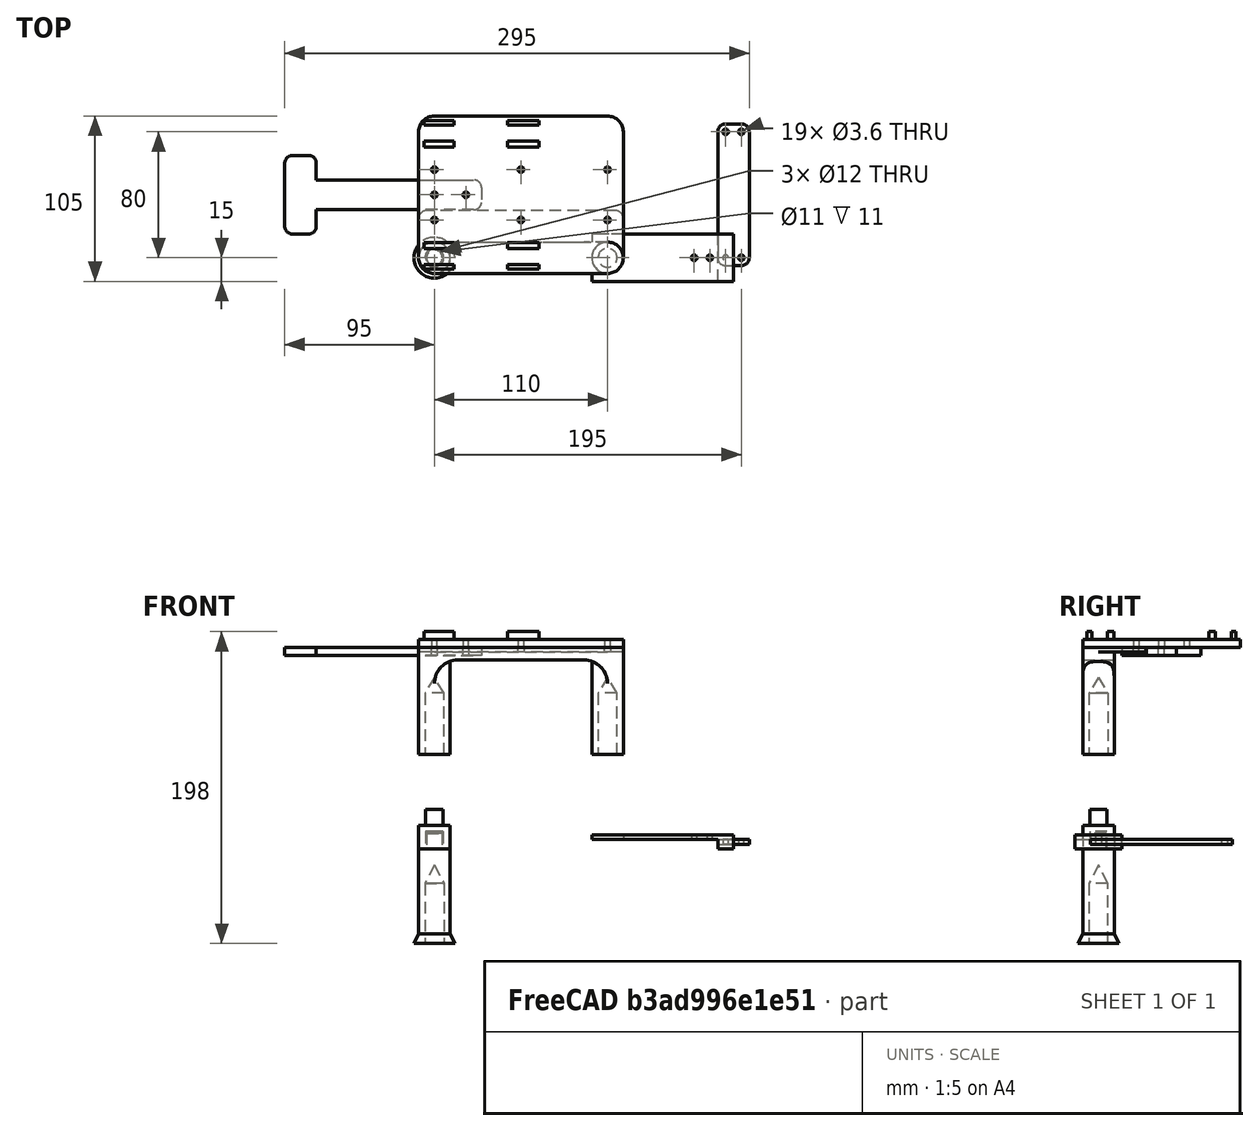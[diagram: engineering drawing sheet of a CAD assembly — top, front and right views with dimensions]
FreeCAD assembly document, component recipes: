
FREECAD ASSEMBLY — COMPONENT RECIPES ("Support_long")

This assembly document has 9 components, labeled P0..P8 below (a component is one placed body or linked part). 9 of them carry a construction recipe — the FreeCAD feature program that regenerates the part from scratch, quoted from this document or its linked companion documents; the rest are supplied as boundary geometry only. No exploded tour is included for this assembly.
COMPONENT P0 — recipe-attached ("Top", modeled in this document).
Construction recipe (the document's own serialized feature program — sketch geometry with constraints, then the solid features built on it; lengths are millimeters unless a unit is written):

FEATURE [Sketcher::SketchObject] Sketch
  ArcFitTolerance = 0
  AttachmentSupport = -> [XY_Plane]
  FullyConstrained = true
  MakeInternals = false
  MapMode = 5
  sketch-geometry (29):
    g0: LineSegment [constr] StartX=0 StartY=100 StartZ=0 EndX=130 EndY=100 EndZ=0
    g1: LineSegment [constr] StartX=130 StartY=100 StartZ=0 EndX=130 EndY=0 EndZ=0
    g2: LineSegment [constr] StartX=130 StartY=0 StartZ=0 EndX=0 EndY=0 EndZ=0
    g3: LineSegment [constr] StartX=0 StartY=0 StartZ=0 EndX=0 EndY=100 EndZ=0
    g4: LineSegment [constr] StartX=10 StartY=66 StartZ=0 EndX=120 EndY=66 EndZ=0
    g5: LineSegment [constr] StartX=120 StartY=66 StartZ=0 EndX=120 EndY=34 EndZ=0
    g6: LineSegment [constr] StartX=120 StartY=34 StartZ=0 EndX=10 EndY=34 EndZ=0
    g7: LineSegment [constr] StartX=10 StartY=34 StartZ=0 EndX=10 EndY=66 EndZ=0
    g8: LineSegment [constr] StartX=130 StartY=100 StartZ=0 EndX=120 EndY=66 EndZ=0
    g9: LineSegment [constr] StartX=120 StartY=34 StartZ=0 EndX=130 EndY=0 EndZ=0
    g10: LineSegment [constr] StartX=10 StartY=66 StartZ=0 EndX=0 EndY=100 EndZ=0
    g11: Circle CenterX=120 CenterY=66 CenterZ=0 NormalX=0 NormalY=0 NormalZ=1 AngleXU=0 Radius=1.8
    g12: Circle CenterX=120 CenterY=34 CenterZ=0 NormalX=0 NormalY=0 NormalZ=1 AngleXU=0 Radius=1.8
    g13: Circle CenterX=10 CenterY=34 CenterZ=0 NormalX=0 NormalY=0 NormalZ=1 AngleXU=0 Radius=1.8
    g14: Circle CenterX=10 CenterY=66 CenterZ=0 NormalX=0 NormalY=0 NormalZ=1 AngleXU=0 Radius=1.8
    g15: Circle CenterX=10 CenterY=50 CenterZ=0 NormalX=0 NormalY=0 NormalZ=1 AngleXU=0 Radius=1.8
    g16: Circle CenterX=30 CenterY=50 CenterZ=0 NormalX=0 NormalY=0 NormalZ=1 AngleXU=0 Radius=1.8
    g17: LineSegment [constr] StartX=0 StartY=100 StartZ=0 EndX=10 EndY=50 EndZ=0
    g18: LineSegment [constr] StartX=10 StartY=50 StartZ=0 EndX=0 EndY=0 EndZ=0
    g19: LineSegment StartX=0 StartY=90 StartZ=0 EndX=0 EndY=10 EndZ=0
    g20: LineSegment StartX=10 StartY=0 StartZ=0 EndX=120 EndY=0 EndZ=0
    g21: LineSegment StartX=130 StartY=10 StartZ=0 EndX=130 EndY=90 EndZ=0
    g22: LineSegment StartX=120 StartY=100 StartZ=0 EndX=10 EndY=100 EndZ=0
    g23: ArcOfCircle CenterX=10 CenterY=90 CenterZ=0 NormalX=0 NormalY=0 NormalZ=1 AngleXU=0 Radius=10 StartAngle=1.5708 EndAngle=3.14159
    g24: ArcOfCircle CenterX=120 CenterY=90 CenterZ=0 NormalX=0 NormalY=0 NormalZ=1 AngleXU=0 Radius=10 StartAngle=0 EndAngle=1.5708
    g25: ArcOfCircle CenterX=120 CenterY=10 CenterZ=0 NormalX=0 NormalY=0 NormalZ=1 AngleXU=0 Radius=10 StartAngle=4.71239 EndAngle=6.28319
    g26: ArcOfCircle CenterX=10 CenterY=10 CenterZ=0 NormalX=0 NormalY=0 NormalZ=1 AngleXU=0 Radius=10 StartAngle=3.14159 EndAngle=4.71239
    g27: Circle CenterX=65 CenterY=66 CenterZ=0 NormalX=0 NormalY=0 NormalZ=1 AngleXU=0 Radius=1.8
    g28: Circle CenterX=65 CenterY=34 CenterZ=0 NormalX=0 NormalY=0 NormalZ=1 AngleXU=0 Radius=1.8
  constraints (82):
    c: Coincident(g0,g1)
    c: Coincident(g1,g2)
    c: Coincident(g2,g3)
    c: Coincident(g3,g0)
    c: Horizontal(g0)
    c: Horizontal(g2)
    c: Vertical(g1)
    c: Vertical(g3)
    c: DistanceY(g1,g1) = 100
    c: DistanceX(g2,g2) = 130
    c: DistanceX(g2) = 0
    c: DistanceY(g2) = 0
    c: Coincident(g4,g5)
    c: Coincident(g5,g6)
    c: Coincident(g6,g7)
    c: Coincident(g7,g4)
    c: Horizontal(g4)
    c: Horizontal(g6)
    c: Vertical(g5)
    c: Vertical(g7)
    c: DistanceX(g4,g4) = 110
    c: DistanceY(g7,g7) = 32
    c: Coincident(g8,g0)
    c: Coincident(g8,g4)
    c: Coincident(g9,g5)
    c: Coincident(g9,g1)
    c: Coincident(g10,g4)
    c: Coincident(g10,g0)
    c: Equal(g10,g8)
    c: Equal(g8,g9)
    c: Coincident(g11,g4)
    c: Coincident(g12,g5)
    c: Coincident(g13,g6)
    c: Coincident(g14,g4)
    c: Equal(g14,g13)
    c: Equal(g13,g11)
    c: Equal(g11,g12)
    c: Radius(g14) = 1.8
    c: DistanceY(g16,g15) = 0
    c: DistanceX(g15,g16) = 20
    c: DistanceX(g2,g15) = 10
    c: Coincident(g17,g0)
    c: Coincident(g17,g15)
    c: Coincident(g18,g15)
    c: Coincident(g18,g2)
    c: Equal(g18,g17)
    c: Equal(g16,g15)
    c: Radius(g16) = 1.8
    c: Vertical(g19)
    c: Vertical(g21)
    c: Horizontal(g20)
    c: Horizontal(g22)
    c: Coincident(g23,g22)
    c: Coincident(g23,g19)
    c: Coincident(g24,g22)
    c: Coincident(g24,g21)
    c: Coincident(g25,g21)
    c: Coincident(g25,g20)
    c: Coincident(g26,g19)
    c: Coincident(g26,g20)
    c: DistanceX(g19,g2) = 0
    c: DistanceX(g19,g21) = 130
    c: DistanceY(g20,g2) = 0
    c: DistanceY(g20,g22) = 100
    c: DistanceX(g22,g23) = 0
    c: DistanceX(g24,g22) = 0
    c: DistanceX(g20,g25) = 0
    c: DistanceX(g20,g26) = 0
    c: DistanceY(g23,g19) = 0
    c: DistanceY(g24,g21) = 0
    c: DistanceY(g21,g25) = 0
    c: DistanceY(g19,g26) = 0
    c: Equal(g23,g24)
    c: Equal(g24,g25)
    c: Equal(g25,g26)
    c: Radius(g23) = 10
    c: DistanceY(g27,g4) = 0
    c: DistanceY(g5,g28) = 0
    c: DistanceX(g27,g28) = 0
    c: Equal(g27,g28)
    c: Equal(g28,g14)
    c: DistanceX(g27,g4) = 55
FEATURE [PartDesign::Pad] Pad
  Direction = (0,0,1)
  Length = 5
  Length2 = 10
  Profile = -> Sketch
  ReferenceAxis = -> Sketch [N_Axis]
  Suppressed = false
  Type = 0
FEATURE [Sketcher::SketchObject] Sketch001
  ArcFitTolerance = 0
  AttachmentOffset = pos=(0,0,5) rot=(0,0,1;0rad)
  AttachmentSupport = -> [XY_Plane]
  FullyConstrained = true
  MakeInternals = false
  MapMode = 5
  Placement = pos=(0,0,5) rot=(0,0,1;0rad)
  sketch-geometry (39):
    g0: LineSegment StartX=56.5 StartY=84.25 StartZ=0 EndX=76.5 EndY=84.25 EndZ=0
    g1: LineSegment StartX=76.5 StartY=84.25 StartZ=0 EndX=76.5 EndY=80.25 EndZ=0
    g2: LineSegment StartX=76.5 StartY=80.25 StartZ=0 EndX=56.5 EndY=80.25 EndZ=0
    g3: LineSegment StartX=56.5 StartY=80.25 StartZ=0 EndX=56.5 EndY=84.25 EndZ=0
    g4: LineSegment StartX=56.5 StartY=19.75 StartZ=0 EndX=76.5 EndY=19.75 EndZ=0
    g5: LineSegment StartX=76.5 StartY=19.75 StartZ=0 EndX=76.5 EndY=15.75 EndZ=0
    g6: LineSegment StartX=76.5 StartY=15.75 StartZ=0 EndX=56.5 EndY=15.75 EndZ=0
    g7: LineSegment StartX=56.5 StartY=15.75 StartZ=0 EndX=56.5 EndY=19.75 EndZ=0
    g8: LineSegment [constr] StartX=80 StartY=100 StartZ=0 EndX=0 EndY=100 EndZ=0
    g9: LineSegment [constr] StartX=0 StartY=100 StartZ=0 EndX=0 EndY=0 EndZ=0
    g10: LineSegment [constr] StartX=0 StartY=0 StartZ=0 EndX=80 EndY=0 EndZ=0
    g11: LineSegment [constr] StartX=80 StartY=0 StartZ=0 EndX=80 EndY=100 EndZ=0
    g12: LineSegment StartX=3.5 StartY=84.25 StartZ=0 EndX=22.5 EndY=84.25 EndZ=0
    g13: LineSegment StartX=22.5 StartY=84.25 StartZ=0 EndX=22.5 EndY=80.25 EndZ=0
    g14: LineSegment StartX=22.5 StartY=80.25 StartZ=0 EndX=3.5 EndY=80.25 EndZ=0
    g15: LineSegment StartX=3.5 StartY=80.25 StartZ=0 EndX=3.5 EndY=84.25 EndZ=0
    g16: LineSegment StartX=3.5 StartY=19.75 StartZ=0 EndX=22.5 EndY=19.75 EndZ=0
    g17: LineSegment StartX=22.5 StartY=19.75 StartZ=0 EndX=22.5 EndY=15.75 EndZ=0
    g18: LineSegment StartX=22.5 StartY=15.75 StartZ=0 EndX=3.5 EndY=15.75 EndZ=0
    g19: LineSegment StartX=3.5 StartY=15.75 StartZ=0 EndX=3.5 EndY=19.75 EndZ=0
    g20: LineSegment [constr] StartX=3.5 StartY=84.25 StartZ=0 EndX=0 EndY=100 EndZ=0
    g21: LineSegment [constr] StartX=76.5 StartY=84.25 StartZ=0 EndX=80 EndY=100 EndZ=0
    g22: LineSegment [constr] StartX=76.5 StartY=15.75 StartZ=0 EndX=80 EndY=0 EndZ=0
    g23: LineSegment StartX=3.5 StartY=97.25 StartZ=0 EndX=22.5 EndY=97.25 EndZ=0
    g24: LineSegment StartX=22.5 StartY=97.25 StartZ=0 EndX=22.5 EndY=94.25 EndZ=0
    g25: LineSegment StartX=22.5 StartY=94.25 StartZ=0 EndX=3.5 EndY=94.25 EndZ=0
    g26: LineSegment StartX=3.5 StartY=94.25 StartZ=0 EndX=3.5 EndY=97.25 EndZ=0
    g27: LineSegment StartX=56.5 StartY=97.25 StartZ=0 EndX=76.5 EndY=97.25 EndZ=0
    g28: LineSegment StartX=76.5 StartY=97.25 StartZ=0 EndX=76.5 EndY=94.25 EndZ=0
    g29: LineSegment StartX=76.5 StartY=94.25 StartZ=0 EndX=56.5 EndY=94.25 EndZ=0
    g30: LineSegment StartX=56.5 StartY=94.25 StartZ=0 EndX=56.5 EndY=97.25 EndZ=0
    g31: LineSegment StartX=56.5 StartY=5.75 StartZ=0 EndX=76.5 EndY=5.75 EndZ=0
    g32: LineSegment StartX=76.5 StartY=5.75 StartZ=0 EndX=76.5 EndY=2.75 EndZ=0
    g33: LineSegment StartX=76.5 StartY=2.75 StartZ=0 EndX=56.5 EndY=2.75 EndZ=0
    g34: LineSegment StartX=56.5 StartY=2.75 StartZ=0 EndX=56.5 EndY=5.75 EndZ=0
    g35: LineSegment StartX=22.5 StartY=5.75 StartZ=0 EndX=3.5 EndY=5.75 EndZ=0
    g36: LineSegment StartX=3.5 StartY=5.75 StartZ=0 EndX=3.5 EndY=2.75 EndZ=0
    g37: LineSegment StartX=3.5 StartY=2.75 StartZ=0 EndX=22.5 EndY=2.75 EndZ=0
    g38: LineSegment StartX=22.5 StartY=2.75 StartZ=0 EndX=22.5 EndY=5.75 EndZ=0
  constraints (114):
    c: Coincident(g0,g1)
    c: Coincident(g1,g2)
    c: Coincident(g2,g3)
    c: Coincident(g3,g0)
    c: Horizontal(g0)
    c: Horizontal(g2)
    c: Vertical(g1)
    c: Vertical(g3)
    c: Coincident(g4,g5)
    c: Coincident(g5,g6)
    c: Coincident(g6,g7)
    c: Coincident(g7,g4)
    c: Horizontal(g4)
    c: Horizontal(g6)
    c: Vertical(g5)
    c: Vertical(g7)
    c: DistanceY(g1,g1) = 4
    c: DistanceY(g5,g5) = 4
    c: DistanceY(g4,g1) = 60.5
    c: Coincident(g8,g9)
    c: Coincident(g9,g10)
    c: Coincident(g10,g11)
    c: Coincident(g11,g8)
    c: Horizontal(g8)
    c: Horizontal(g10)
    c: Vertical(g9)
    c: Vertical(g11)
    c: DistanceX(g8,g8) = 80
    c: DistanceY(g11,g11) = 100
    c: DistanceX(g9) = 0
    c: DistanceY(g9) = 0
    c: DistanceX(g2,g2) = 20
    c: DistanceX(g1,g4) = 0
    c: DistanceX(g2,g4) = 0
    c: Coincident(g12,g13)
    c: Coincident(g13,g14)
    c: Coincident(g14,g15)
    c: Coincident(g15,g12)
    c: Horizontal(g12)
    c: Horizontal(g14)
    c: Vertical(g13)
    c: Vertical(g15)
    c: Coincident(g16,g17)
    c: Coincident(g17,g18)
    c: Coincident(g18,g19)
    c: Coincident(g19,g16)
    c: Horizontal(g16)
    c: Horizontal(g18)
    c: Vertical(g17)
    c: Vertical(g19)
    c: DistanceX(g12,g12) = 19
    c: DistanceY(g12,g0) = 0
    c: DistanceY(g13,g2) = 0
    c: DistanceY(g4,g16) = 0
    c: DistanceY(g17,g6) = 0
    c: DistanceX(g13,g16) = 0
    c: DistanceX(g14,g16) = 0
    c: DistanceX(g12,g0) = 34
    c: Coincident(g20,g12)
    c: Coincident(g20,g8)
    c: Coincident(g21,g0)
    c: Coincident(g21,g8)
    c: Coincident(g22,g5)
    c: Coincident(g22,g10)
    c: Equal(g20,g21)
    c: Equal(g21,g22)
    c: Coincident(g23,g24)
    c: Coincident(g24,g25)
    c: Coincident(g25,g26)
    c: Coincident(g26,g23)
    c: Horizontal(g23)
    c: Horizontal(g25)
    c: Vertical(g24)
    c: Vertical(g26)
    c: Coincident(g27,g28)
    c: Coincident(g28,g29)
    c: Coincident(g29,g30)
    c: Coincident(g30,g27)
    c: Horizontal(g27)
    c: Horizontal(g29)
    c: Vertical(g28)
    c: Vertical(g30)
    c: Coincident(g31,g32)
    c: Coincident(g32,g33)
    c: Coincident(g33,g34)
    c: Coincident(g34,g31)
    c: Horizontal(g31)
    c: Horizontal(g33)
    c: Vertical(g32)
    c: Vertical(g34)
    c: Coincident(g35,g36)
    c: Coincident(g36,g37)
    c: Coincident(g37,g38)
    c: Coincident(g38,g35)
    c: Horizontal(g35)
    c: Horizontal(g37)
    c: Vertical(g36)
    c: Vertical(g38)
    c: DistanceY(g31,g6) = 10
    c: DistanceY(g35,g31) = 0
    c: DistanceY(g37,g33) = 0
    c: DistanceY(g0,g29) = 10
    c: DistanceY(g24,g29) = 0
    c: DistanceY(g27,g23) = 0
    c: DistanceY(g28,g28) = 3
    c: DistanceY(g32,g32) = 3
    c: DistanceX(g31,g5) = 0
    c: DistanceX(g6,g31) = 0
    c: DistanceX(g18,g35) = 0
    c: DistanceX(g35,g17) = 0
    c: DistanceX(g24,g12) = 0
    c: DistanceX(g12,g25) = 0
    c: DistanceX(g0,g29) = 0
    c: DistanceX(g0,g28) = 0
FEATURE [PartDesign::Pad] Pad001
  BaseFeature = -> Pad
  Direction = (0,0,1)
  Length = 5
  Length2 = 10
  Profile = -> Sketch001
  ReferenceAxis = -> Sketch001 [N_Axis]
  Suppressed = false
  Type = 0
FEATURE [PartDesign::Body] Body  label="Top"
  AllowCompound = false
  Group = -> [Sketch,Pad,Sketch001,Pad001]
  Origin = -> Origin
  Tip = -> Pad001
COMPONENT P1 — recipe-attached ("Stick", modeled in this document).
Construction recipe (the document's own serialized feature program — sketch geometry with constraints, then the solid features built on it; lengths are millimeters unless a unit is written):

FEATURE [Sketcher::SketchObject] Sketch007
  ArcFitTolerance = 0
  AttachmentSupport = -> [XY_Plane003]
  FullyConstrained = true
  MakeInternals = false
  MapMode = 5
  sketch-geometry (18):
    g0: LineSegment StartX=-65 StartY=59.5 StartZ=0 EndX=35 EndY=59.5 EndZ=0
    g1: LineSegment StartX=40 StartY=54.5 StartZ=0 EndX=40 EndY=45.5 EndZ=0
    g2: LineSegment StartX=35 StartY=40.5 StartZ=0 EndX=-65 EndY=40.5 EndZ=0
    g3: LineSegment StartX=-85 StartY=30 StartZ=0 EndX=-85 EndY=70 EndZ=0
    g4: Circle CenterX=30 CenterY=50 CenterZ=0 NormalX=0 NormalY=0 NormalZ=1 AngleXU=0 Radius=1.8
    g5: Circle CenterX=10 CenterY=50 CenterZ=0 NormalX=0 NormalY=0 NormalZ=1 AngleXU=0 Radius=1.8
    g6: LineSegment [constr] StartX=30 StartY=50 StartZ=0 EndX=40 EndY=54.5 EndZ=0
    g7: LineSegment [constr] StartX=30 StartY=50 StartZ=0 EndX=40 EndY=45.5 EndZ=0
    g8: ArcOfCircle CenterX=35 CenterY=54.5 CenterZ=0 NormalX=0 NormalY=0 NormalZ=1 AngleXU=0 Radius=5 StartAngle=5e-16 EndAngle=1.5708
    g9: ArcOfCircle CenterX=35 CenterY=45.5 CenterZ=0 NormalX=0 NormalY=0 NormalZ=1 AngleXU=0 Radius=5 StartAngle=4.71239 EndAngle=6.28319
    g10: ArcOfCircle CenterX=-80 CenterY=70 CenterZ=0 NormalX=0 NormalY=0 NormalZ=1 AngleXU=0 Radius=5 StartAngle=1.5708 EndAngle=3.14159
    g11: ArcOfCircle CenterX=-80 CenterY=30 CenterZ=0 NormalX=0 NormalY=0 NormalZ=1 AngleXU=0 Radius=5 StartAngle=3.14159 EndAngle=4.71239
    g12: LineSegment StartX=-65 StartY=59.5 StartZ=0 EndX=-65 EndY=70 EndZ=0
    g13: LineSegment StartX=-70 StartY=75 StartZ=0 EndX=-80 EndY=75 EndZ=0
    g14: LineSegment StartX=-65 StartY=40.5 StartZ=0 EndX=-65 EndY=30 EndZ=0
    g15: LineSegment StartX=-70 StartY=25 StartZ=0 EndX=-80 EndY=25 EndZ=0
    g16: ArcOfCircle CenterX=-70 CenterY=70 CenterZ=0 NormalX=0 NormalY=0 NormalZ=1 AngleXU=0 Radius=5 StartAngle=0 EndAngle=1.5708
    g17: ArcOfCircle CenterX=-70 CenterY=30 CenterZ=0 NormalX=0 NormalY=0 NormalZ=1 AngleXU=0 Radius=5 StartAngle=4.71239 EndAngle=6.28319
  constraints (58):
    c: Horizontal(g0)
    c: Horizontal(g2)
    c: Vertical(g1)
    c: Vertical(g3)
    c: DistanceX(g1) = 40
    c: DistanceY(g5,g4) = 0
    c: DistanceX(g5,g4) = 20
    c: DistanceX(g-1,g5) = 10
    c: Equal(g4,g5)
    c: Radius(g4) = 1.8
    c: DistanceY(g2,g0) = 19
    c: DistanceY(g-1,g5) = 50
    c: Coincident(g6,g4)
    c: Coincident(g6,g1)
    c: Coincident(g7,g4)
    c: Coincident(g7,g1)
    c: Equal(g7,g6)
    c: DistanceX(g3,g1) = 125
    c: Coincident(g8,g0)
    c: Coincident(g8,g1)
    c: Coincident(g9,g1)
    c: Coincident(g9,g2)
    c: DistanceX(g0,g8) = 0
    c: DistanceX(g2,g9) = 0
    c: DistanceY(g8,g1) = 0
    c: DistanceY(g9,g1) = 0
    c: Equal(g8,g9)
    c: Radius(g8) = 5
    c: Coincident(g10,g3)
    c: Coincident(g11,g3)
    c: DistanceY(g3,g10) = 0
    c: DistanceY(g3,g11) = 0
    c: Equal(g10,g11)
    c: Radius(g10) = 5
    c: DistanceX(g10,g10) = 0
    c: DistanceX(g11,g11) = 0
    c: Coincident(g0,g12)
    c: Vertical(g12)
    c: Horizontal(g13)
    c: Coincident(g2,g14)
    c: Vertical(g14)
    c: Horizontal(g15)
    c: DistanceX(g0,g2) = 0
    c: Coincident(g13,g10)
    c: Coincident(g11,g15)
    c: Equal(g12,g14)
    c: DistanceY(g3,g3) = 40
    c: DistanceY(g16,g16) = 0
    c: DistanceX(g16,g16) = 0
    c: DistanceX(g17,g17) = 0
    c: DistanceY(g17,g17) = 0
    c: Equal(g16,g17)
    c: Coincident(g16,g13)
    c: Coincident(g12,g16)
    c: Coincident(g17,g14)
    c: Coincident(g17,g15)
    c: Radius(g16) = 5
    c: DistanceX(g13,g13) = 10
FEATURE [PartDesign::Pad] Pad006
  Direction = (0,0,1)
  Length = 5
  Length2 = 10
  Profile = -> Sketch007
  ReferenceAxis = -> Sketch007 [N_Axis]
  Reversed = true
  Suppressed = false
  Type = 0
FEATURE [PartDesign::Body] Body003  label="Stick"
  AllowCompound = false
  Group = -> [Sketch007,Pad006]
  Origin = -> Origin003
  Tip = -> Pad006
COMPONENT P2 — recipe-attached ("Cross", modeled in this document).
Construction recipe (the document's own serialized feature program — sketch geometry with constraints, then the solid features built on it; lengths are millimeters unless a unit is written):

FEATURE [Sketcher::SketchObject] Sketch010
  ArcFitTolerance = 1e-06
  AttachmentSupport = -> [XY_Plane005]
  FullyConstrained = true
  MakeInternals = false
  MapMode = 5
  sketch-geometry (14):
    g0: LineSegment StartX=-5 StartY=80 StartZ=0 EndX=-5 EndY=0 EndZ=0
    g1: LineSegment StartX=-9e-16 StartY=-5 StartZ=0 EndX=10 EndY=-5 EndZ=0
    g2: LineSegment StartX=15 StartY=-1.2e-15 StartZ=0 EndX=15 EndY=80 EndZ=0
    g3: LineSegment StartX=10 StartY=85 StartZ=0 EndX=0 EndY=85 EndZ=0
    g4: ArcOfCircle CenterX=0 CenterY=80 CenterZ=0 NormalX=0 NormalY=0 NormalZ=1 AngleXU=0 Radius=5 StartAngle=1.5708 EndAngle=3.14159
    g5: ArcOfCircle CenterX=0 CenterY=0 CenterZ=0 NormalX=0 NormalY=0 NormalZ=1 AngleXU=0 Radius=5 StartAngle=3.14159 EndAngle=4.71239
    g6: ArcOfCircle CenterX=10 CenterY=0 CenterZ=0 NormalX=0 NormalY=0 NormalZ=1 AngleXU=0 Radius=5 StartAngle=4.71239 EndAngle=6.28319
    g7: ArcOfCircle CenterX=10 CenterY=80 CenterZ=0 NormalX=0 NormalY=0 NormalZ=1 AngleXU=0 Radius=5 StartAngle=1e-16 EndAngle=1.5708
    g8: GeomPoint [constr] X=-5 Y=85 Z=0
    g9: GeomPoint [constr] X=15 Y=-5 Z=0
    g10: Circle CenterX=10 CenterY=80 CenterZ=0 NormalX=0 NormalY=0 NormalZ=1 AngleXU=0 Radius=1.8
    g11: Circle CenterX=0 CenterY=80 CenterZ=0 NormalX=0 NormalY=0 NormalZ=1 AngleXU=0 Radius=1.8
    g12: Circle CenterX=0 CenterY=0 CenterZ=0 NormalX=0 NormalY=0 NormalZ=1 AngleXU=0 Radius=1.8
    g13: Circle CenterX=10 CenterY=0 CenterZ=0 NormalX=0 NormalY=0 NormalZ=1 AngleXU=0 Radius=1.8
  constraints (32):
    c: Tangent(g0,g4) = -1.5708
    c: Tangent(g0,g5) = -1.5708
    c: Tangent(g1,g5) = -1.5708
    c: Tangent(g1,g6) = -1.5708
    c: Tangent(g2,g6) = -1.5708
    c: Tangent(g2,g7) = -1.5708
    c: Tangent(g3,g7) = -1.5708
    c: Tangent(g3,g4) = -1.5708
    c: Vertical(g0)
    c: Vertical(g2)
    c: Horizontal(g1)
    c: Horizontal(g3)
    c: Equal(g4,g5)
    c: Equal(g5,g6)
    c: Equal(g6,g7)
    c: PointOnObject(g8,g0)
    c: PointOnObject(g8,g3)
    c: PointOnObject(g9,g1)
    c: PointOnObject(g9,g2)
    c: Radius(g7) = 5
    c: DistanceX(g4,g7) = 10
    c: DistanceY(g6,g7) = 80
    c: DistanceX(g5) = 0
    c: DistanceY(g5) = 0
    c: Coincident(g10,g7)
    c: Coincident(g11,g4)
    c: Coincident(g12,g5)
    c: Coincident(g13,g6)
    c: Equal(g10,g11)
    c: Equal(g11,g12)
    c: Equal(g12,g13)
    c: Radius(g10) = 1.8
FEATURE [PartDesign::Pad] Pad008
  Direction = (0,0,1)
  Length = 3
  Length2 = 10
  Profile = -> Sketch010
  ReferenceAxis = -> Sketch010 [N_Axis]
  Suppressed = false
  Type = 0
FEATURE [PartDesign::Body] Body005  label="Cross"
  AllowCompound = false
  Group = -> [Sketch010,Pad008]
  Origin = -> Origin005
  Placement = pos=(195,10,-125) rot=(0,0,1;0rad)
  Tip = -> Pad008
COMPONENT P3 — recipe-attached ("Segment", modeled in this document).
Construction recipe (the document's own serialized feature program — sketch geometry with constraints, then the solid features built on it; lengths are millimeters unless a unit is written):

FEATURE [PartDesign::AdditiveCylinder] Cylinder003
  Angle = 360
  AttacherType = Attacher::AttachEngine3D
  AttachmentOffset = pos=(10,0,-127) rot=(0,0,1;1.5708rad)
  AttachmentSupport = -> [XY_Plane006]
  FirstAngle = 0
  Height = 15
  MapMode = 5
  Placement = pos=(10,0,-127) rot=(0,0,1;1.5708rad)
  Radius = 10
  SecondAngle = 0
  Suppressed = false
FEATURE [PartDesign::AdditiveCylinder] Cylinder004
  Angle = 360
  AttacherType = Attacher::AttachEngine3D
  AttachmentOffset = pos=(10,0,-112) rot=(0,0,1;0rad)
  AttachmentSupport = -> [XY_Plane006]
  BaseFeature = -> Cylinder003
  FirstAngle = 0
  Height = 10
  MapMode = 5
  Placement = pos=(10,0,-112) rot=(0,0,1;0rad)
  Radius = 5.5
  SecondAngle = 0
  Suppressed = false
FEATURE [PartDesign::SubtractiveCylinder] Cylinder005
  Angle = 360
  AttacherType = Attacher::AttachEngine3D
  AttachmentOffset = pos=(10,0,-127) rot=(0,0,1;0rad)
  AttachmentSupport = -> [XY_Plane006]
  BaseFeature = -> Cylinder004
  FirstAngle = 0
  Height = 11
  MapMode = 5
  Placement = pos=(10,0,-127) rot=(0,0,1;0rad)
  Radius = 5.5
  SecondAngle = 0
  Suppressed = false
FEATURE [PartDesign::Body] Body006  label="Segment"
  AllowCompound = false
  Group = -> [Cylinder003,Cylinder004,Cylinder005]
  Origin = -> Origin006
  Placement = pos=(10,2.2e-15,-1) rot=(0,0,1;1.5708rad)
  Tip = -> Cylinder005
COMPONENT P4 — recipe-attached ("Mid2", modeled in this document).
Construction recipe (the document's own serialized feature program — sketch geometry with constraints, then the solid features built on it; lengths are millimeters unless a unit is written):

FEATURE [Sketcher::SketchObject] Sketch002
  ArcFitTolerance = 0
  AttachmentSupport = -> [XY_Plane001]
  FullyConstrained = true
  MakeInternals = false
  MapMode = 5
  sketch-geometry (16):
    g0: LineSegment [constr] StartX=0 StartY=40 StartZ=0 EndX=130 EndY=40 EndZ=0
    g1: LineSegment [constr] StartX=130 StartY=40 StartZ=0 EndX=130 EndY=10 EndZ=0
    g2: LineSegment StartX=120 StartY=0 StartZ=0 EndX=10 EndY=0 EndZ=0
    g3: LineSegment [constr] StartX=0 StartY=10 StartZ=0 EndX=0 EndY=40 EndZ=0
    g4: Circle CenterX=120 CenterY=34 CenterZ=0 NormalX=0 NormalY=0 NormalZ=1 AngleXU=0 Radius=1.8
    g5: Circle CenterX=10 CenterY=34 CenterZ=0 NormalX=0 NormalY=0 NormalZ=1 AngleXU=0 Radius=1.8
    g6: LineSegment [constr] StartX=120 StartY=34 StartZ=0 EndX=130 EndY=40 EndZ=0
    g7: LineSegment [constr] StartX=10 StartY=34 StartZ=0 EndX=0 EndY=40 EndZ=0
    g8: ArcOfCircle CenterX=120 CenterY=10 CenterZ=0 NormalX=0 NormalY=0 NormalZ=1 AngleXU=0 Radius=10 StartAngle=4.71239 EndAngle=6.28319
    g9: ArcOfCircle CenterX=10 CenterY=10 CenterZ=0 NormalX=0 NormalY=0 NormalZ=1 AngleXU=0 Radius=10 StartAngle=3.14159 EndAngle=4.71239
    g10: LineSegment StartX=0 StartY=35 StartZ=0 EndX=0 EndY=10 EndZ=0
    g11: LineSegment StartX=130 StartY=10 StartZ=0 EndX=130 EndY=35 EndZ=0
    g12: LineSegment StartX=125 StartY=40 StartZ=0 EndX=5 EndY=40 EndZ=0
    g13: ArcOfCircle CenterX=5 CenterY=35 CenterZ=0 NormalX=0 NormalY=0 NormalZ=1 AngleXU=0 Radius=5 StartAngle=1.5708 EndAngle=3.14159
    g14: ArcOfCircle CenterX=125 CenterY=35 CenterZ=0 NormalX=0 NormalY=0 NormalZ=1 AngleXU=0 Radius=5 StartAngle=5e-16 EndAngle=1.5708
    g15: Circle CenterX=65 CenterY=34 CenterZ=0 NormalX=0 NormalY=0 NormalZ=1 AngleXU=0 Radius=1.8
  constraints (51):
    c: Coincident(g0,g1)
    c: Coincident(g3,g0)
    c: Horizontal(g0)
    c: Horizontal(g2)
    c: Vertical(g1)
    c: Vertical(g3)
    c: DistanceY(g2) = 0
    c: DistanceY(g5,g4) = 0
    c: Equal(g5,g4)
    c: Radius(g5) = 1.8
    c: Coincident(g6,g4)
    c: Coincident(g6,g0)
    c: Coincident(g7,g5)
    c: Coincident(g7,g0)
    c: Equal(g7,g6)
    c: DistanceX(g5,g4) = 110
    c: DistanceY(g2,g5) = 34
    c: DistanceY(g2,g0) = 40
    c: Coincident(g8,g1)
    c: Coincident(g8,g2)
    c: Radius(g8) = 10
    c: DistanceX(g8,g2) = 0
    c: DistanceY(g1,g8) = 0
    c: DistanceX(g0,g-1) = 0
    c: Coincident(g9,g3)
    c: Coincident(g9,g2)
    c: DistanceX(g2,g9) = 0
    c: DistanceY(g3,g9) = 0
    c: Equal(g9,g8)
    c: DistanceX(g-1,g0) = 130
    c: Vertical(g10)
    c: Vertical(g11)
    c: Horizontal(g12)
    c: DistanceY(g12,g0) = 0
    c: DistanceX(g0,g11) = 0
    c: DistanceX(g10,g0) = 0
    c: DistanceY(g3,g10) = 0
    c: Coincident(g13,g12)
    c: Coincident(g13,g10)
    c: Coincident(g14,g12)
    c: Coincident(g14,g11)
    c: DistanceY(g1,g11) = 0
    c: DistanceY(g14,g11) = 0
    c: DistanceY(g13,g10) = 0
    c: DistanceX(g12,g13) = 0
    c: DistanceX(g14,g12) = 0
    c: Equal(g13,g14)
    c: Radius(g13) = 5
    c: DistanceY(g15,g4) = 0
    c: Equal(g15,g5)
    c: DistanceX(g15,g4) = 55
FEATURE [PartDesign::Pad] Pad002
  Direction = (0,0,1)
  Length = 3
  Length2 = 10
  Profile = -> Sketch002
  ReferenceAxis = -> Sketch002 [N_Axis]
  Reversed = true
  Suppressed = false
  Type = 0
FEATURE [Sketcher::SketchObject] Sketch003
  ArcFitTolerance = 0
  AttachmentOffset = pos=(0,0,-3) rot=(0,0,1;0rad)
  AttachmentSupport = -> [XY_Plane001]
  FullyConstrained = true
  MakeInternals = false
  MapMode = 5
  Placement = pos=(0,0,-3) rot=(0,0,1;0rad)
  sketch-geometry (2):
    g0: Circle CenterX=10 CenterY=10 CenterZ=0 NormalX=0 NormalY=0 NormalZ=1 AngleXU=0 Radius=10
    g1: Circle CenterX=120 CenterY=10 CenterZ=0 NormalX=0 NormalY=0 NormalZ=1 AngleXU=0 Radius=10
  constraints (6):
    c: Tangent(g0,g-1)
    c: Radius(g0) = 10
    c: DistanceY(g0,g1) = 0
    c: Tangent(g1,g-1)
    c: DistanceX(g0,g1) = 110
    c: Tangent(g0,g-2)
FEATURE [PartDesign::Pad] Pad003
  BaseFeature = -> Pad002
  Direction = (0,0,1)
  Length = 65
  Length2 = 10
  Profile = -> Sketch003
  ReferenceAxis = -> Sketch003 [N_Axis]
  Reversed = true
  Suppressed = false
  Type = 0
FEATURE [Sketcher::SketchObject] Sketch004
  ArcFitTolerance = 0
  AttachmentSupport = -> [XZ_Plane001]
  FullyConstrained = true
  MakeInternals = false
  MapMode = 5
  Placement = pos=(0,0,0) rot=(1,0,0;1.5708rad)
  sketch-geometry (6):
    g0: LineSegment StartX=10 StartY=-3 StartZ=0 EndX=120 EndY=-3 EndZ=0
    g1: LineSegment StartX=120 StartY=-3 StartZ=0 EndX=120 EndY=-23 EndZ=0
    g2: LineSegment StartX=10 StartY=-23 StartZ=0 EndX=10 EndY=-3 EndZ=0
    g3: ArcOfCircle CenterX=25 CenterY=-23 CenterZ=0 NormalX=0 NormalY=0 NormalZ=1 AngleXU=0 Radius=15 StartAngle=1.5708 EndAngle=3.14159
    g4: ArcOfCircle CenterX=105 CenterY=-23 CenterZ=0 NormalX=0 NormalY=0 NormalZ=1 AngleXU=0 Radius=15 StartAngle=0 EndAngle=1.5708
    g5: LineSegment StartX=25 StartY=-8 StartZ=0 EndX=105 EndY=-8 EndZ=0
  constraints (18):
    c: Coincident(g0,g1)
    c: Coincident(g2,g0)
    c: Horizontal(g0)
    c: Vertical(g1)
    c: Vertical(g2)
    c: DistanceY(g2,g2) = 20
    c: DistanceX(g0,g0) = 110
    c: DistanceX(g0) = 10
    c: DistanceY(g0) = -3
    c: Coincident(g3,g2)
    c: Coincident(g4,g1)
    c: Horizontal(g5)
    c: DistanceY(g2,g3) = 0
    c: DistanceY(g4,g1) = 0
    c: Radius(g4) = 15
    c: DistanceY(g3,g4) = 0
    c: Tangent(g5,g4) = 1.5708
    c: Tangent(g5,g3) = 1.5708
FEATURE [PartDesign::Pad] Pad004
  BaseFeature = -> Pad003
  Direction = (0,-1,2e-16)
  Length = 20
  Length2 = 10
  Profile = -> Sketch004
  ReferenceAxis = -> Sketch004 [N_Axis]
  Reversed = true
  Suppressed = false
  Type = 0
FEATURE [Sketcher::SketchObject] Sketch008
  ArcFitTolerance = 0
  AttachmentOffset = pos=(0,0,-68) rot=(0,0,1;0rad)
  AttachmentSupport = -> [XY_Plane001]
  FullyConstrained = true
  MakeInternals = false
  MapMode = 5
  Placement = pos=(0,0,-68) rot=(0,0,1;0rad)
  sketch-geometry (2):
    g0: Circle CenterX=10 CenterY=10 CenterZ=0 NormalX=0 NormalY=0 NormalZ=1 AngleXU=0 Radius=6
    g1: Circle CenterX=120 CenterY=10 CenterZ=0 NormalX=0 NormalY=0 NormalZ=1 AngleXU=0 Radius=6
  constraints (6):
    c: DistanceY(g0,g1) = 0
    c: DistanceX(g0,g1) = 110
    c: DistanceX(g0) = 10
    c: DistanceY(g0) = 10
    c: Radius(g0) = 6
    c: Equal(g0,g1)
FEATURE [PartDesign::Pocket] Pocket
  BaseFeature = -> Pad004
  Direction = (0,0,-1)
  Length = 39
  Length2 = 5
  Profile = -> Sketch008
  ReferenceAxis = -> Sketch008 [N_Axis]
  Reversed = true
  Suppressed = false
  Type = 0
FEATURE [PartDesign::SubtractiveCone] Cone001
  Angle = 360
  AttacherType = Attacher::AttachEngine3D
  AttachmentOffset = pos=(10,10,-29) rot=(0,0,1;0rad)
  AttachmentSupport = -> [XY_Plane001]
  BaseFeature = -> Pocket
  Height = 10
  MapMode = 5
  Placement = pos=(10,10,-29) rot=(0,0,1;0rad)
  Radius1 = 6
  Radius2 = 0
  Suppressed = false
FEATURE [PartDesign::SubtractiveCone] Cone002
  Angle = 360
  AttacherType = Attacher::AttachEngine3D
  AttachmentOffset = pos=(120,10,-29) rot=(0,0,1;0rad)
  AttachmentSupport = -> [XY_Plane001]
  BaseFeature = -> Cone001
  Height = 10
  MapMode = 5
  Placement = pos=(120,10,-29) rot=(0,0,1;0rad)
  Radius1 = 6
  Radius2 = 0
  Suppressed = false
FEATURE [PartDesign::Body] Body001  label="Mid1"
  AllowCompound = false
  Group = -> [Sketch002,Pad002,Sketch003,Pad003,Sketch004,Pad004,Sketch008,Pocket,Cone001,Cone002]
  Origin = -> Origin001
  Tip = -> Cone002
COMPONENT P5 — recipe-attached ("Leg2", modeled in this document).
Construction recipe (the document's own serialized feature program — sketch geometry with constraints, then the solid features built on it; lengths are millimeters unless a unit is written):

FEATURE [PartDesign::AdditiveCylinder] Cylinder
  Angle = 360
  AttacherType = Attacher::AttachEngine3D
  AttachmentOffset = pos=(10,0,-127) rot=(0,0,1;1.5708rad)
  AttachmentSupport = -> [XY_Plane002]
  FirstAngle = 0
  Height = 60
  MapMode = 5
  Placement = pos=(10,0,-127) rot=(0,0,1;1.5708rad)
  Radius = 10
  SecondAngle = 0
  Suppressed = false
FEATURE [PartDesign::AdditiveCone] Cone003
  Angle = 360
  AttacherType = Attacher::AttachEngine3D
  AttachmentOffset = pos=(10,0,-127) rot=(0,0,1;0rad)
  AttachmentSupport = -> [XY_Plane002]
  BaseFeature = -> Cylinder
  Height = 26
  MapMode = 5
  Placement = pos=(10,0,-127) rot=(0,0,1;0rad)
  Radius1 = 13
  Radius2 = 0
  Suppressed = false
FEATURE [PartDesign::AdditiveCylinder] Cylinder001
  Angle = 360
  AttacherType = Attacher::AttachEngine3D
  AttachmentOffset = pos=(10,0,-67) rot=(0,0,1;0rad)
  AttachmentSupport = -> [XY_Plane002]
  BaseFeature = -> Cone003
  FirstAngle = 0
  Height = 10
  MapMode = 5
  Placement = pos=(10,0,-67) rot=(0,0,1;0rad)
  Radius = 5
  SecondAngle = 0
  Suppressed = false
FEATURE [PartDesign::SubtractiveCylinder] Cylinder002
  Angle = 360
  AttacherType = Attacher::AttachEngine3D
  AttachmentOffset = pos=(10,0,-127) rot=(0,0,1;0rad)
  AttachmentSupport = -> [XY_Plane002]
  BaseFeature = -> Cylinder001
  FirstAngle = 0
  Height = 38
  MapMode = 5
  Placement = pos=(10,0,-127) rot=(0,0,1;0rad)
  Radius = 6
  SecondAngle = 0
  Suppressed = false
FEATURE [PartDesign::SubtractiveCone] Cone
  Angle = 360
  AttacherType = Attacher::AttachEngine3D
  AttachmentOffset = pos=(10,0,-89) rot=(0,0,1;0rad)
  AttachmentSupport = -> [XY_Plane002]
  BaseFeature = -> Cylinder002
  Height = 12
  MapMode = 5
  Placement = pos=(10,0,-89) rot=(0,0,1;0rad)
  Radius1 = 6
  Radius2 = 0
  Suppressed = false
FEATURE [PartDesign::Body] Body002  label="Leg1"
  AllowCompound = false
  Group = -> [Cylinder,Cone003,Cylinder001,Cylinder002,Cone]
  Origin = -> Origin002
  Placement = pos=(10,2.2e-15,-61) rot=(0,0,1;1.5708rad)
  Tip = -> Cone
COMPONENT P6 — same part as P5; its construction recipe is shown at P5.
COMPONENT P7 — same part as P5; its construction recipe is shown at P5.
COMPONENT P8 — recipe-attached ("Pusher001", modeled in this document).
Construction recipe (the document's own serialized feature program — sketch geometry with constraints, then the solid features built on it; lengths are millimeters unless a unit is written):

FEATURE [Sketcher::SketchObject] Sketch009
  ArcFitTolerance = 1e-06
  AttachmentSupport = -> [XY_Plane004]
  FullyConstrained = true
  MakeInternals = false
  MapMode = 5
  sketch-geometry (10):
    g0: LineSegment StartX=-10 StartY=-15 StartZ=0 EndX=80 EndY=-15 EndZ=0
    g1: LineSegment StartX=80 StartY=-15 StartZ=0 EndX=80 EndY=15 EndZ=0
    g2: LineSegment StartX=80 StartY=15 StartZ=0 EndX=-10 EndY=15 EndZ=0
    g3: LineSegment StartX=-10 StartY=15 StartZ=0 EndX=-10 EndY=10 EndZ=0
    g4: LineSegment StartX=-10 StartY=-15 StartZ=0 EndX=-10 EndY=-10 EndZ=0
    g5: ArcOfCircle CenterX=0 CenterY=0 CenterZ=0 NormalX=0 NormalY=0 NormalZ=1 AngleXU=0 Radius=10 StartAngle=4.71239 EndAngle=7.85398
    g6: LineSegment StartX=8.3e-14 StartY=10 StartZ=0 EndX=-10 EndY=10 EndZ=0
    g7: LineSegment StartX=7.81e-14 StartY=-10 StartZ=0 EndX=-10 EndY=-10 EndZ=0
    g8: Circle CenterX=65 CenterY=0 CenterZ=0 NormalX=0 NormalY=0 NormalZ=1 AngleXU=0 Radius=1.8
    g9: Circle CenterX=55 CenterY=0 CenterZ=0 NormalX=0 NormalY=0 NormalZ=1 AngleXU=0 Radius=1.8
  constraints (29):
    c: Coincident(g0,g1)
    c: Coincident(g1,g2)
    c: Vertical(g1)
    c: Horizontal(g0)
    c: Horizontal(g2)
    c: DistanceX(g2,g2) = 90
    c: Coincident(g3,g2)
    c: Vertical(g3)
    c: Coincident(g4,g0)
    c: Vertical(g4)
    c: DistanceX(g5) = 0
    c: DistanceY(g5) = 0
    c: Radius(g5) = 10
    c: Coincident(g6,g3)
    c: Coincident(g7,g4)
    c: Horizontal(g6)
    c: Horizontal(g7)
    c: DistanceX(g4,g3) = 0
    c: Tangent(g6,g5) = -1.5708
    c: Tangent(g7,g5) = 1.5708
    c: DistanceX(g2,g5) = 10
    c: DistanceY(g5,g2) = 15
    c: DistanceY(g0,g5) = 15
    c: PointOnObject(g8,g-1)
    c: PointOnObject(g9,g-1)
    c: Equal(g9,g8)
    c: Radius(g8) = 1.8
    c: DistanceX(g5,g9) = 55
    c: DistanceX(g9,g8) = 10
FEATURE [PartDesign::Pad] Pad007
  Direction = (0,0,1)
  Length = 3
  Length2 = 10
  Profile = -> Sketch009
  ReferenceAxis = -> Sketch009 [N_Axis]
  Suppressed = false
  Type = 0
FEATURE [PartDesign::AdditiveBox] Box
  AttacherType = Attacher::AttachEngine3D
  AttachmentOffset = pos=(70,-15,-6) rot=(0,0,1;0rad)
  AttachmentSupport = -> [XY_Plane004]
  BaseFeature = -> Pad007
  Height = 6
  Length = 10
  MapMode = 5
  Placement = pos=(70,-15,-6) rot=(0,0,1;0rad)
  Suppressed = false
  Width = 30
FEATURE [PartDesign::Body] Body004  label="Pusher"
  AllowCompound = false
  Group = -> [Sketch009,Pad007,Box]
  Origin = -> Origin004
  Placement = pos=(120,10,-122) rot=(0,0,1;0rad)
  Tip = -> Box
PROVENANCE & LICENSES
A FreeCAD (.FCStd) document from a public repository crawl; recipes are the document's own serialized feature recipes (and, for linked parts, companion documents' recipes).
License: as declared in the source repository (recorded in the dataset sidecar).
